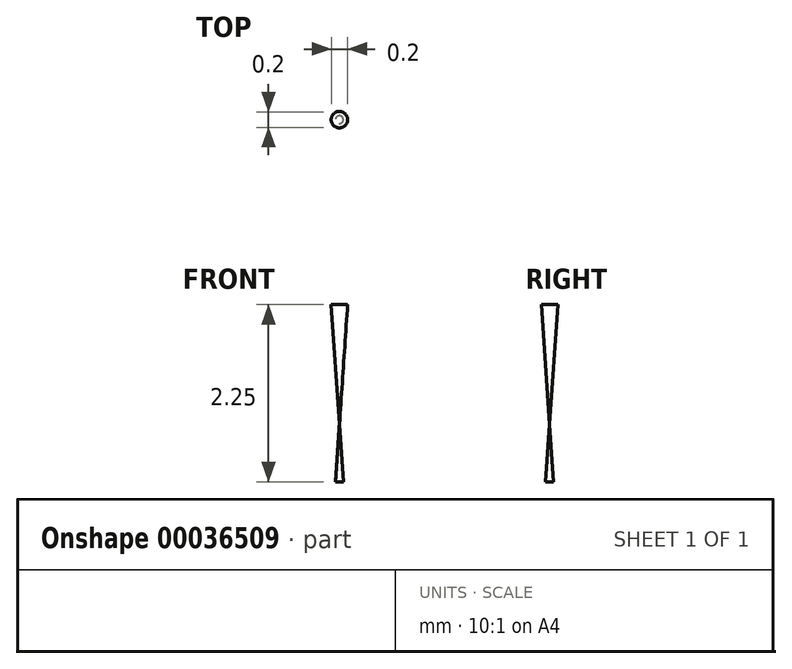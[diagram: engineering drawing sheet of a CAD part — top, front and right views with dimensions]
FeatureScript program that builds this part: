
annotation { "Feature Type Name" : "Feature", "Feature Type Description" : "" }
export const myFeature = defineFeature(function(context is Context, id is Id, definition is map)
    precondition{}
    {
        {
            var Q0;
            Q0=qCreatedBy(makeId("Right.planeOp"),FACE);
            var sketch = newSketch(context, id + "F0", { "sketchPlane" : qUnion([Q0])});
            skLineSegment(sketch, "E0", {"start": v(0, 0) * mm, "end": v(0, 2.25) * mm});
            skLineSegment(sketch, "E1", {"start": v(0, 2.25) * mm, "end": v(0.1, 2.25) * mm});
            skLineSegment(sketch, "E2", {"start": v(0.1, 2.25) * mm, "end": v(-0.05, 0) * mm});
            skLineSegment(sketch, "E3", {"start": v(0, 0) * mm, "end": v(-0.05, 0) * mm});
            skSolve(sketch);
        }
        {
            var Q0;
            Q0 = qSketchRegion(id + "F0", true);
            var Q1;
            Q1=sQuery(id+"F0.wireOp",EDGE,"E0");
            revolve(context, id + "F1", {"entities" : qUnion([Q0]), "axis" : qUnion([Q1]), "revolveType" : RevolveType.FULL});
        }
    });
